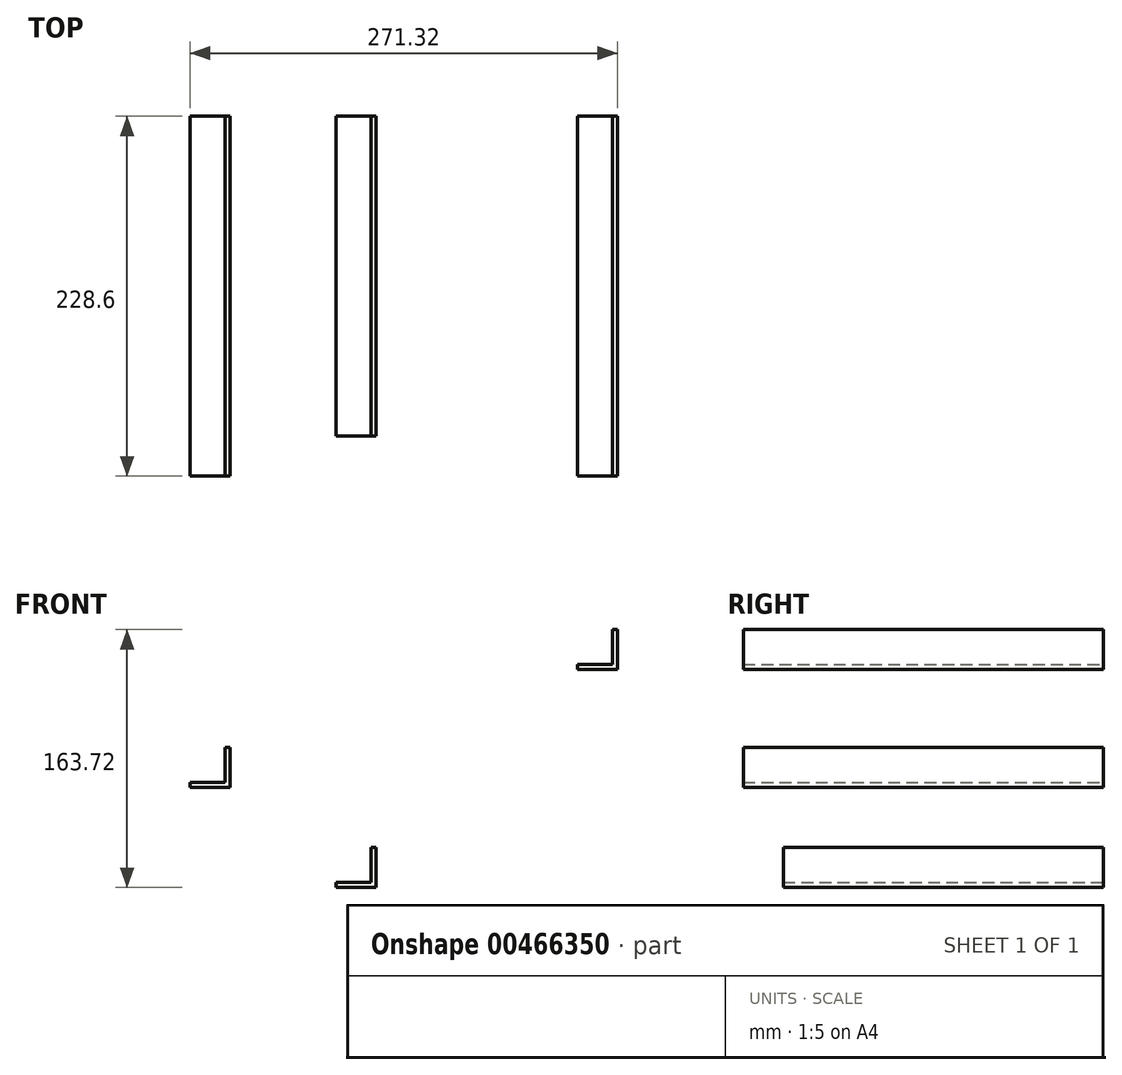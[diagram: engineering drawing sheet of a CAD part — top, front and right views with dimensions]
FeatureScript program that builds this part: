
annotation { "Feature Type Name" : "Feature", "Feature Type Description" : "" }
export const myFeature = defineFeature(function(context is Context, id is Id, definition is map)
    precondition{}
    {
        {
            var Q0;
            Q0=qCreatedBy(makeId("Front.planeOp"),FACE);
            var sketch = newSketch(context, id + "F0", { "sketchPlane" : qUnion([Q0])});
            skLineSegment(sketch, "E0", {"start": v(490.67, 169.62) * mm, "end": v(465.27, 169.62) * mm});
            skLineSegment(sketch, "E1", {"start": v(490.67, 169.62) * mm, "end": v(490.67, 195.02) * mm});
            skLineSegment(sketch, "E2", {"start": v(465.27, 169.62) * mm, "end": v(465.27, 172.8) * mm});
            skLineSegment(sketch, "E3", {"start": v(465.27, 172.8) * mm, "end": v(487.5, 172.8) * mm});
            skLineSegment(sketch, "E4", {"start": v(487.5, 172.8) * mm, "end": v(487.5, 195.02) * mm});
            skLineSegment(sketch, "E5", {"start": v(487.5, 195.02) * mm, "end": v(490.67, 195.02) * mm});
            skSolve(sketch);
        }
        {
            var Q0;
            Q0 = qSketchRegion(id + "F0", true);
            extrude(context, id + "F1", {"entities" : qUnion([Q0]), "depth" : 228.6 * mm});
        }
        {
            var Q0;
            Q0=qCreatedBy(makeId("Front.planeOp"),FACE);
            var sketch = newSketch(context, id + "F2", { "sketchPlane" : qUnion([Q0])});
            skLineSegment(sketch, "E6", {"start": v(337.28, 31.3) * mm, "end": v(311.88, 31.3) * mm});
            skLineSegment(sketch, "E7", {"start": v(337.28, 31.3) * mm, "end": v(337.28, 56.7) * mm});
            skLineSegment(sketch, "E8", {"start": v(337.28, 56.7) * mm, "end": v(334.1, 56.7) * mm});
            skLineSegment(sketch, "E9", {"start": v(334.1, 56.7) * mm, "end": v(334.1, 34.48) * mm});
            skLineSegment(sketch, "E10", {"start": v(311.88, 34.48) * mm, "end": v(334.1, 34.48) * mm});
            skLineSegment(sketch, "E11", {"start": v(311.88, 31.3) * mm, "end": v(311.88, 34.48) * mm});
            skSolve(sketch);
        }
        {
            var Q0;
            Q0=makeQuery(id+"F2.imprint","IMPRINT",FACE,{"disambiguationData":[TD([[makeQuery(id+"F2.imprint","IMPRINT",EDGE,{"derivedFrom":sQuery(id+"F2.wireOp",EDGE,"E6")}),-1.0]])]});
            extrude(context, id + "F3", {"entities" : qUnion([Q0]), "depth" : 203.2 * mm});
        }
        {
            var Q0;
            Q0=qCreatedBy(makeId("Front.planeOp"),FACE);
            var sketch = newSketch(context, id + "F4", { "sketchPlane" : qUnion([Q0])});
            skLineSegment(sketch, "E12", {"start": v(244.75, 94.84) * mm, "end": v(219.35, 94.84) * mm});
            skLineSegment(sketch, "E13", {"start": v(244.75, 94.84) * mm, "end": v(244.75, 120.24) * mm});
            skLineSegment(sketch, "E14", {"start": v(244.75, 120.24) * mm, "end": v(241.57, 120.24) * mm});
            skLineSegment(sketch, "E15", {"start": v(241.57, 120.24) * mm, "end": v(241.57, 98.02) * mm});
            skLineSegment(sketch, "E16", {"start": v(219.35, 98.02) * mm, "end": v(219.35, 94.84) * mm});
            skLineSegment(sketch, "E17", {"start": v(241.57, 98.02) * mm, "end": v(219.35, 98.02) * mm});
            skSolve(sketch);
        }
        {
            var Q0;
            Q0=makeQuery(id+"F4.imprint","IMPRINT",FACE,{"disambiguationData":[TD([[makeQuery(id+"F4.imprint","IMPRINT",EDGE,{"derivedFrom":sQuery(id+"F4.wireOp",EDGE,"E12")}),-1.0]])]});
            extrude(context, id + "F5", {"entities" : qUnion([Q0]), "depth" : 228.6 * mm});
        }
    });
